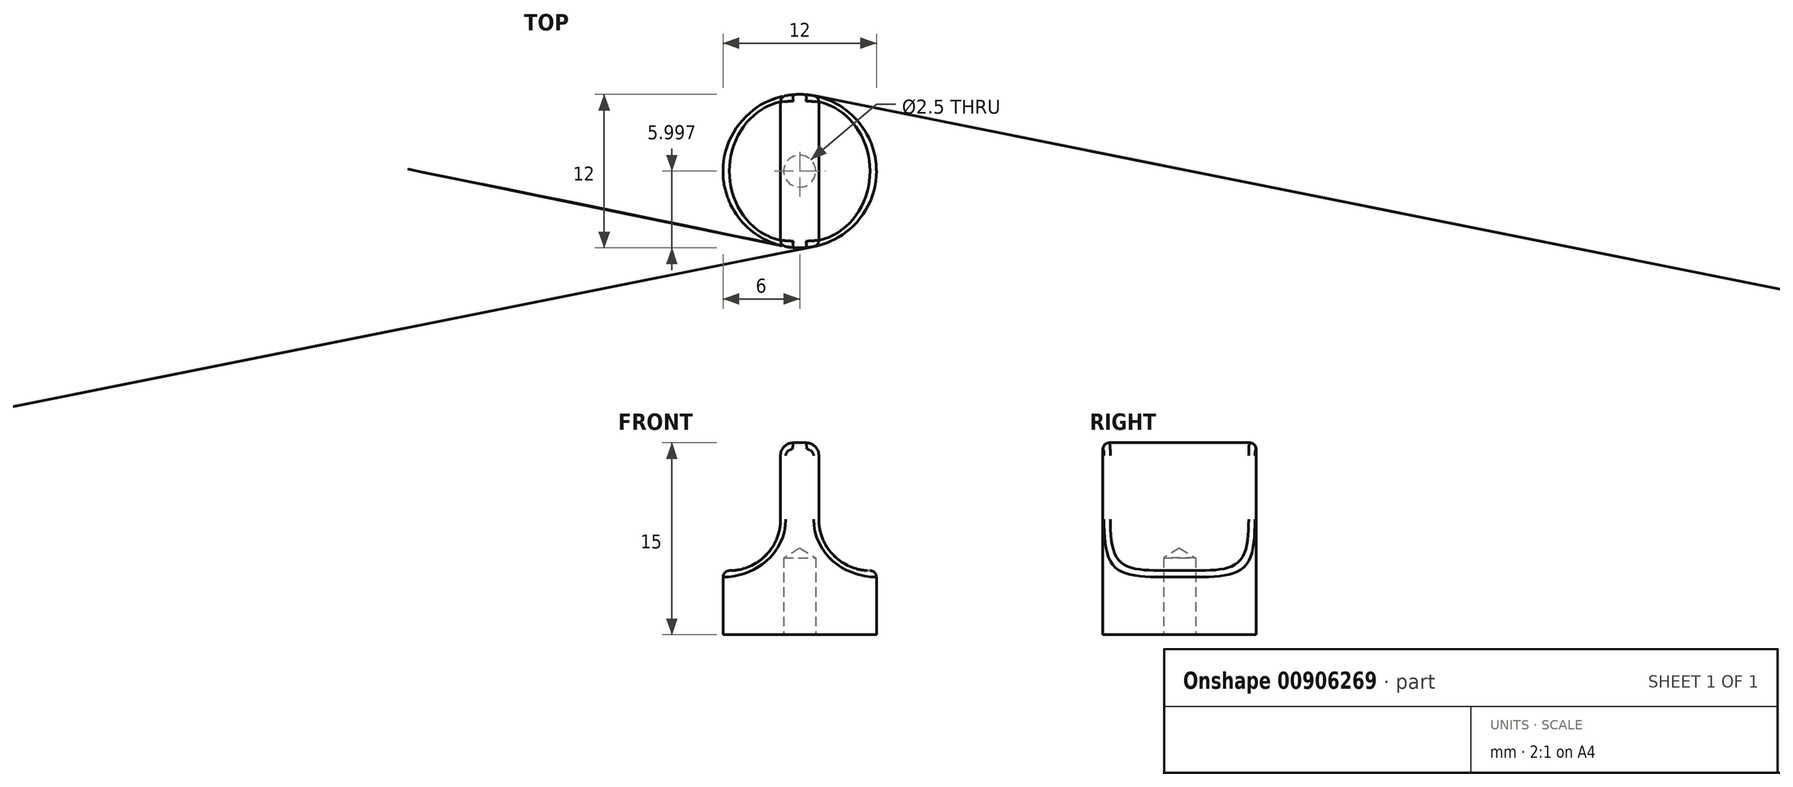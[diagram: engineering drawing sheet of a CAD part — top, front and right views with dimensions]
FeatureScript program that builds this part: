
annotation { "Feature Type Name" : "Feature", "Feature Type Description" : "" }
export const myFeature = defineFeature(function(context is Context, id is Id, definition is map)
    precondition{}
    {
        {
            var Q0;
            Q0=qCreatedBy(makeId("Top.planeOp"),FACE);
            var sketch = newSketch(context, id + "F0", { "sketchPlane" : qUnion([Q0])});
            skCircle(sketch, "E0", {"center": v(-32.66, 35.12) * mm, "radius": 6 * mm});
            skLineSegment(sketch, "E1", {"start": v(-31.16, 35.12) * mm, "end": v(-31.16, 40.93) * mm});
            skLineSegment(sketch, "E2", {"start": v(-31.16, 40.93) * mm, "end": v(-31.16, 29.3) * mm});
            skLineSegment(sketch, "E3", {"start": v(-34.16, 35.12) * mm, "end": v(-34.16, 40.93) * mm});
            skLineSegment(sketch, "E4", {"start": v(-34.16, 40.93) * mm, "end": v(-34.16, 29.3) * mm});
            skSolve(sketch);
        }
        {
            var Q0;
            {var subQ0=sQuery(id+"F0.wireOp",EDGE,"E3");Q0=makeQuery(id+"F0.imprint","IMPRINT",FACE,{"disambiguationData":[TD([[makeQuery(id+"F0.imprint","IMPRINT",EDGE,{"derivedFrom":subQ0}),1.0]])]});}
            var Q1;
            {var subQ0=sQuery(id+"F0.wireOp",EDGE,"E1");Q1=makeQuery(id+"F0.imprint","IMPRINT",FACE,{"disambiguationData":[TD([[makeQuery(id+"F0.imprint","IMPRINT",EDGE,{"derivedFrom":subQ0}),1.0]])]});}
            var Q2;
            {var subQ0=sQuery(id+"F0.wireOp",EDGE,"E1");Q2=makeQuery(id+"F0.imprint","IMPRINT",FACE,{"disambiguationData":[TD([[makeQuery(id+"F0.imprint","IMPRINT",EDGE,{"derivedFrom":subQ0}),-1.0]])]});}
            extrude(context, id + "F1", {"entities" : qUnion([Q0, Q1, Q2]), "depth" : 5 * mm, "offsetDistance" : 25 * mm});
        }
        {
            var Q0;
            {var subQ0=sQuery(id+"F0.wireOp",EDGE,"E1");Q0=makeQuery(id+"F0.imprint","IMPRINT",FACE,{"disambiguationData":[TD([[makeQuery(id+"F0.imprint","IMPRINT",EDGE,{"derivedFrom":subQ0}),1.0]])]});}
            extrude(context, id + "F2", {"entities" : qUnion([Q0]), "operationType" : NewBodyOperationType.ADD, "depth" : 15 * mm, "offsetDistance" : 25 * mm});
        }
        {
            var Q0;
            Q0=makeQuery(id+"F2.boolean.opBoolean","INTERSECT",EDGE,{"derivedFrom":[makeQuery(id+"F1.opExtrude","CAP_FACE",FACE,{"disambiguationData":[OSD([sQuery(id+"F0.wireOp",EDGE,"E0")])],"isStart":false}),makeQuery(id+"F2.opExtrude","SWEPT_FACE",FACE,{"disambiguationData":[OSD([sQuery(id+"F0.wireOp",EDGE,"E3"),sQuery(id+"F0.wireOp",EDGE,"E4")])]})]});
            var Q1;
            Q1=makeQuery(id+"F2.boolean.opBoolean","INTERSECT",EDGE,{"derivedFrom":[makeQuery(id+"F1.opExtrude","CAP_FACE",FACE,{"disambiguationData":[OSD([sQuery(id+"F0.wireOp",EDGE,"E0")])],"isStart":false}),makeQuery(id+"F2.opExtrude","SWEPT_FACE",FACE,{"disambiguationData":[OSD([sQuery(id+"F0.wireOp",EDGE,"E1"),sQuery(id+"F0.wireOp",EDGE,"E2")])]})]});
            fillet(context, id + "F3", {"entities" : qUnion([Q0, Q1]), "radius" : 4 * mm, "tangentPropagation" : true, "allowEdgeOverflow" : false});
        }
        {
            var Q0;
            Q0=makeQuery(id+"F2.opExtrude","CAP_EDGE",EDGE,{"disambiguationData":[OSD([sQuery(id+"F0.wireOp",EDGE,"E1"),sQuery(id+"F0.wireOp",EDGE,"E2")])],"isStart":false});
            var Q1;
            Q1=makeQuery(id+"F2.opExtrude","CAP_EDGE",EDGE,{"disambiguationData":[OSD([sQuery(id+"F0.wireOp",EDGE,"E3"),sQuery(id+"F0.wireOp",EDGE,"E4")])],"isStart":false});
            fillet(context, id + "F4", {"entities" : qUnion([Q0, Q1]), "radius" : 1 * mm, "tangentPropagation" : true, "allowEdgeOverflow" : false});
        }
        {
            var Q0;
            Q0=makeQuery(id+"F2.opExtrude","SWEPT_EDGE",EDGE,{"disambiguationData":[OSD([sQuery(id+"F0.wireOp",EDGE,"E0"),sQuery(id+"F0.wireOp",EDGE,"E1")])]});
            fillet(context, id + "F5", {"entities" : qUnion([Q0]), "radius" : 0.5 * mm, "tangentPropagation" : true, "allowEdgeOverflow" : false});
        }
        {
            var Q0;
            Q0=sQuery(id+"F0.wireOp",VERTEX,"E0.center");
            var Q1;
            Q1=makeQuery(id+"F1.opExtrude","SWEPT_BODY",BODY,{"disambiguationData":[OSD([sQuery(id+"F0.wireOp",EDGE,"E0")])]});
            hole(context, id + "F6", {"style" : HoleStyle.SIMPLE, "endStyle" : HoleEndStyle.BLIND, "oppositeDirection" : true, "standardTappedOrClearance" : lookupTablePath({ "standard" : "ISO", "engagement" : "75%", "pitch" : "0.5 mm", "size" : "M3", "type" : "Tapped" }), "standardBlindInLast" : lookupTablePath({ "standard" : "ISO", "engagement" : "75%", "pitch" : "0.5 mm", "size" : "M3", "type" : "Tapped" }), "holeDiameter" : 2.5 * mm, "majorDiameter" : 3 * mm, "showTappedDepth" : true, "holeDepth" : 6 * mm, "isTappedThrough" : true, "tappedDepth" : 4.5 * mm, "tapClearance" : 3, "startFromSketch" : true, "locations" : qUnion([Q0]), "scope" : qUnion([Q1])});
        }
    });
